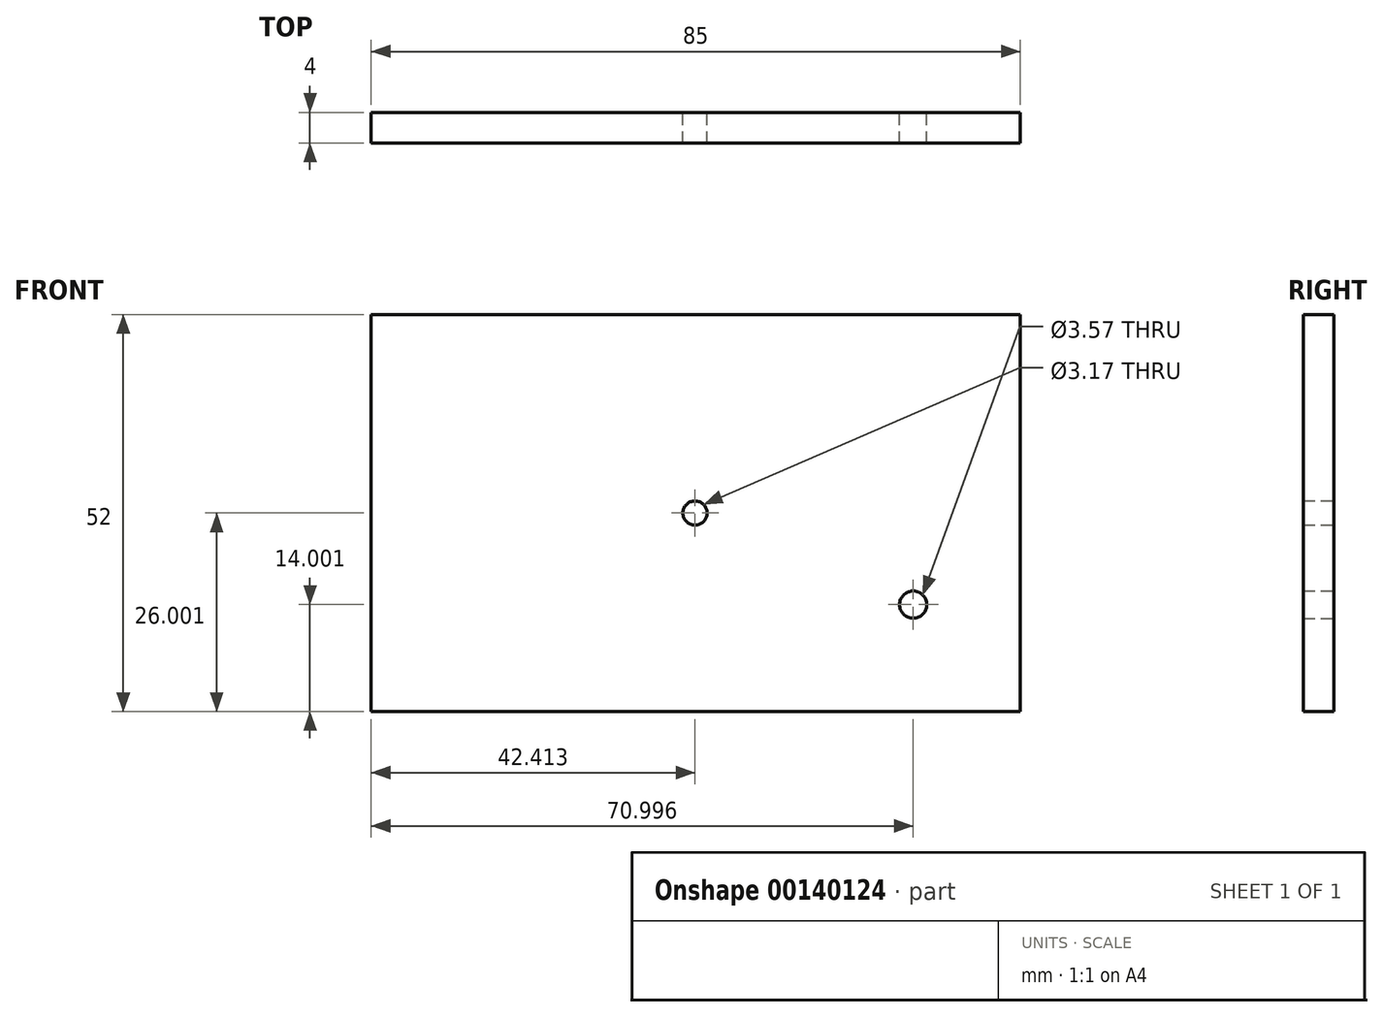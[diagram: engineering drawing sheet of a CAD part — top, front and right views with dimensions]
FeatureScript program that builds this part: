
annotation { "Feature Type Name" : "Feature", "Feature Type Description" : "" }
export const myFeature = defineFeature(function(context is Context, id is Id, definition is map)
    precondition{}
    {
        {
            var Q0;
            Q0=qCreatedBy(makeId("Front.planeOp"),FACE);
            var sketch = newSketch(context, id + "F0", { "sketchPlane" : qUnion([Q0])});
            skLineSegment(sketch, "E0.right", {"start": v(62.14, -25.16) * mm, "end": v(62.14, 26.84) * mm});
            skCircle(sketch, "E1", {"center": v(48.14, -11.16) * mm, "radius": 1.79 * mm});
            skCircle(sketch, "E2", {"center": v(19.55, 0.84) * mm, "radius": 1.59 * mm});
            skLineSegment(sketch, "E3", {"start": v(-22.86, -25.16) * mm, "end": v(-22.86, 26.84) * mm});
            skLineSegment(sketch, "E4", {"start": v(62.14, 26.84) * mm, "end": v(-22.86, 26.84) * mm});
            skLineSegment(sketch, "E5", {"start": v(62.14, -25.16) * mm, "end": v(-22.86, -25.16) * mm});
            skSolve(sketch);
        }
        {
            var Q0;
            Q0=makeQuery(id+"F0.imprint","IMPRINT",FACE,{"disambiguationData":[TD([[makeQuery(id+"F0.imprint","IMPRINT",EDGE,{"derivedFrom":sQuery(id+"F0.wireOp",EDGE,"E0.right")}),1.0]])]});
            extrude(context, id + "F1", {"entities" : qUnion([Q0]), "depth" : 4 * mm});
        }
    });
